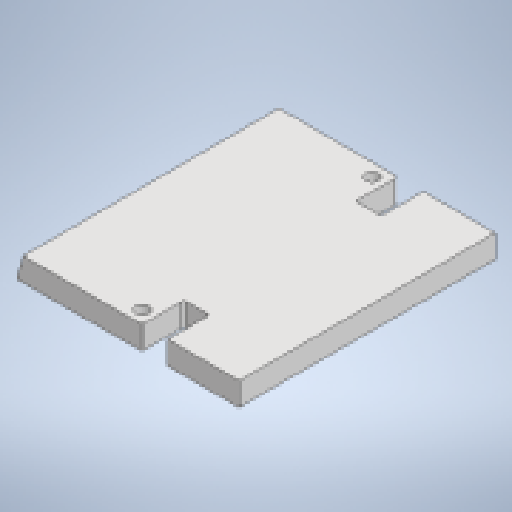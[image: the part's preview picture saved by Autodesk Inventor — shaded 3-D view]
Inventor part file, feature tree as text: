
AUTODESK INVENTOR PART (.ipt)
format: ipt  version: 2023 (Build 270158000, 158)  size: 442,880 bytes
history: native  units: mm
features: reference x24, extrude x7, sketch x7, other x5, projected_geometry x4, fillet x1
ambient origin geometry x8: Origin, YZ Plane, XZ Plane, XY Plane, X Axis, Y Axis, Z Axis, Center Point
bodies: Body1 (feature_tree)
feature tree (48):
  other  "Bryła1"
  extrude  "Wyciągnięcie proste1"  Depth=1.0mm
  extrude  "Wyciągnięcie proste2"  Depth=1.0mm
  extrude  "Wyciągnięcie proste3"  Depth=1.0mm
  extrude  "Wyciągnięcie proste4"  Depth=1.0mm
  extrude  "Wyciągnięcie proste5"  Depth=1.0mm
  extrude  "Wyciągnięcie proste6"  Depth=3.5mm TaperAngle=0.0deg
  fillet  "Zaokrąglenie1"  Radius=1.05mm
  extrude  "Wyciągnięcie proste7"  Depth=3.0mm TaperAngle=0.0deg
  sketch  "Szkic1"
  sketch  "Szkic2"
  projected_geometry  "Pętla rzutowana1"
  sketch  "Szkic3"
  projected_geometry  "Pętla rzutowana2"
  sketch  "Szkic4"
  reference  "Odniesienie1"
  projected_geometry  "Pętla rzutowana3"
  sketch  "Szkic5"
  reference  "Odniesienie2"
  reference  "Odniesienie3"
  reference  "Odniesienie4"
  reference  "Odniesienie5"
  reference  "Odniesienie6"
  reference  "Odniesienie7"
  reference  "Odniesienie8"
  reference  "Odniesienie9"
  reference  "Odniesienie10"
  reference  "Odniesienie11"
  reference  "Odniesienie12"
  reference  "Odniesienie13"
  reference  "Odniesienie14"
  reference  "Odniesienie15"
  reference  "Odniesienie16"
  reference  "Odniesienie17"
  reference  "Odniesienie18"
  reference  "Odniesienie19"
  reference  "Odniesienie20"
  reference  "Odniesienie21"
  sketch  "Szkic6"
  reference  "Odniesienie22"
  reference  "Odniesienie23"
  reference  "Odniesienie24"
  sketch  "Szkic7"
  projected_geometry  "Pętla rzutowana4"
  other  "<userpath>\Documents\PROJECTS - repos\Stratos---MicroSumo\mechanics\byk_alternator.iam"
  other  "byk_alternator.iam"
  other  "noz2:1"
  other  "MikroSumo:2"
